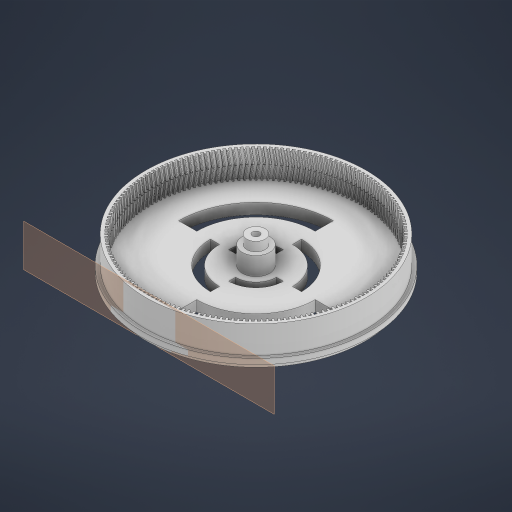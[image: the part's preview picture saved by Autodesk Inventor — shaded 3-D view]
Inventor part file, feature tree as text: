
AUTODESK INVENTOR PART (.ipt)
format: ipt  version: 2023 (Build 270158030, 158C)  size: 2,457,600 bytes
history: native  units: in
note: dims shown in document units (in); Inventor stores cm internally (conversion verified against a paired STEP export)
features: extrude x10, sketch x8, plane x1, fillet x1, pattern_circular x1
ambient origin geometry x8: Origin, YZ Plane, XZ Plane, XY Plane, X Axis, Y Axis, Z Axis, Center Point
bodies: Solid1 (feature_tree)
feature tree (21):
  extrude  "Extrusion1"  Depth=0.2362in TaperAngle=0.0deg
  extrude  "Extrusion2"  Depth=0.2362in TaperAngle=0.0deg
  extrude  "Extrusion3"  Depth=0.315in TaperAngle=0.0deg
  extrude  "Extrusion5"  Depth=1.1811in
  extrude  "Extrusion6"  Depth=1.1811in
  plane  "Work Plane2"
  extrude  "Extrusion8"  Depth=0.0787in
  fillet  "Fillet1"  Radius=0.0787in
  sketch  "Sketch26"  dims[d28=0.1181in d29=0.0in d38=0.0394in]
  extrude  "Extrusion11"  Depth=0.0394in
  extrude  "Extrusion12"  Depth=1.1811in
  extrude  "Extrusion13"  Depth=1.1811in
  pattern_circular  "Circular Pattern3"  Count=2  [1 undecoded]
  extrude  "Extrusion15"  Depth=1.1811in TaperAngle=0.0deg
  sketch  "Sketch2"  dims[d0=9.8425in d1=0.2362in d2=0.0in]
  sketch  "Sketch3"  dims[d3=9.4488in d4=0.2362in d5=0.0in]
  sketch  "Sketch4"  dims[d6=0.315in d7=0.315in d8=0.0in]
  sketch  "Sketch9"  dims[d15=1.1811in d16=0.0in d17=9.252in]
  sketch  "Sketch12"  dims[d18=1.1811in d19=0.0in d24=4.626in]
  sketch  "Sketch17"  dims[d25=0.0787in d26=0.0787in d27=0.0787in]
  sketch  "Sketch28"  dims[d42=1.1811in d43=0.7874in d44=0.3071in d45=0.7874in d46=0.0in d47=1.1811in d48=0.0in d49=0.0in d50=0.0in d51=63.7795in d52=360.0deg d61=1.7717in d62=2.3622in d63=3.1496in d64=3.937in d65=5.1181in d66=6.6929in d67=0.5906in d68=0.0in]
note: 1 required parameter value undecoded (feature->parameter linkage not recoverable at this tier; creation-order binding heuristic only, values carry confidence <= 0.55)
